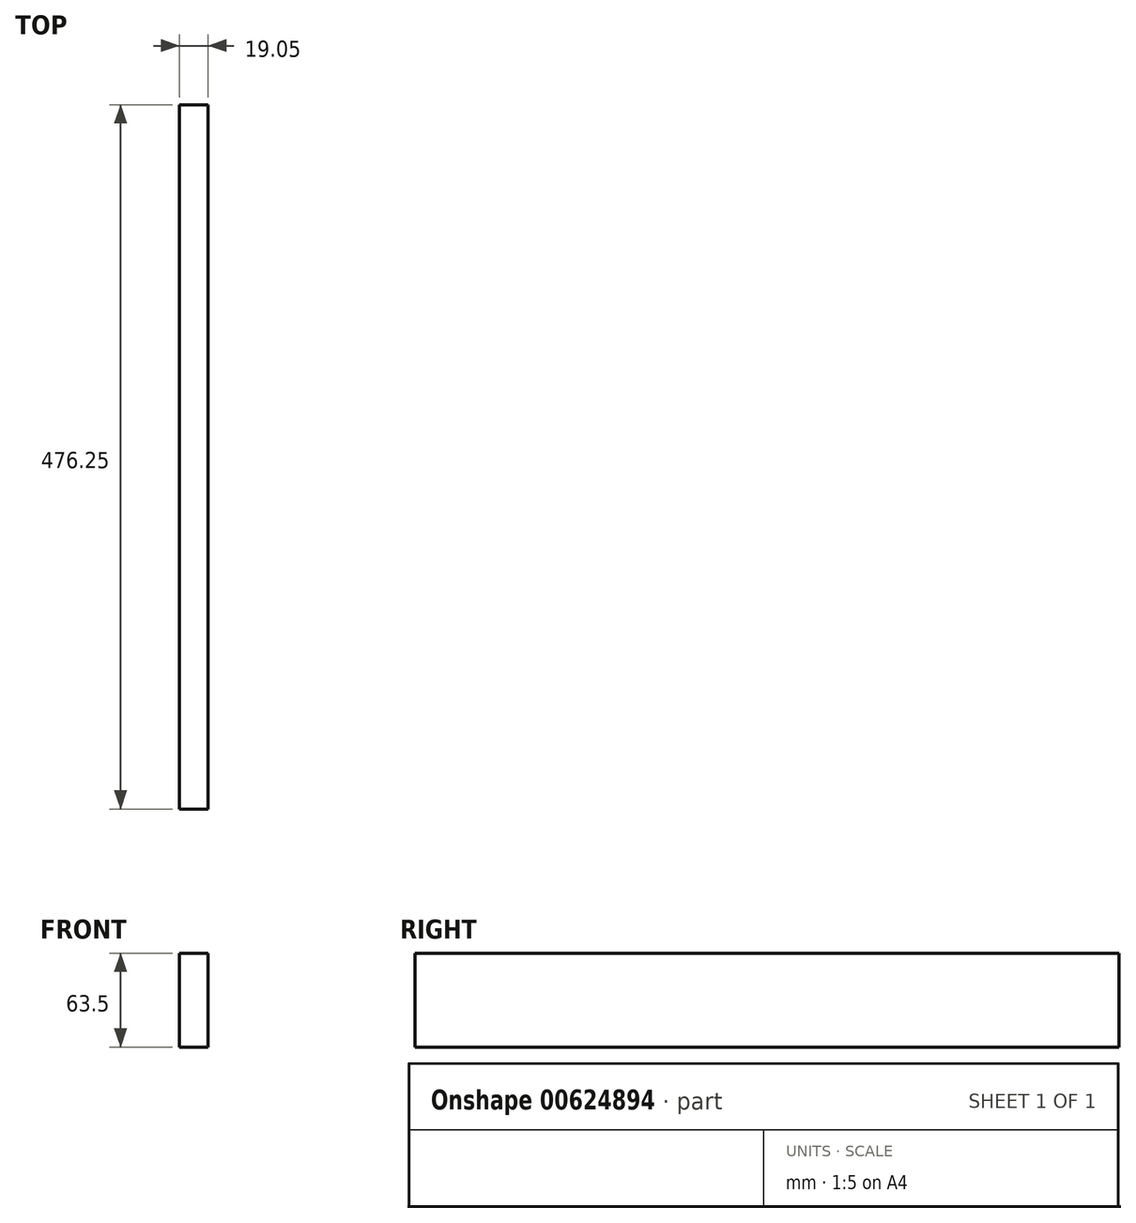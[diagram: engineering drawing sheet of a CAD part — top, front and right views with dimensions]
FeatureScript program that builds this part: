
annotation { "Feature Type Name" : "Feature", "Feature Type Description" : "" }
export const myFeature = defineFeature(function(context is Context, id is Id, definition is map)
    precondition{}
    {
        {
            var Q0;
            Q0=qCreatedBy(makeId("Right.planeOp"),FACE);
            var sketch = newSketch(context, id + "F0", { "sketchPlane" : qUnion([Q0])});
            skLineSegment(sketch, "E0.bottom", {"start": v(0, 0) * mm, "end": v(-476.25, 0) * mm});
            skLineSegment(sketch, "E0.top", {"start": v(0, 63.5) * mm, "end": v(-476.25, 63.5) * mm});
            skLineSegment(sketch, "E0.left", {"start": v(0, 0) * mm, "end": v(0, 63.5) * mm});
            skLineSegment(sketch, "E0.right", {"start": v(-476.25, 0) * mm, "end": v(-476.25, 63.5) * mm});
            skSolve(sketch);
        }
        {
            var Q0;
            Q0=makeQuery(id+"F0.imprint","IMPRINT",FACE,{"disambiguationData":[TD([[makeQuery(id+"F0.imprint","IMPRINT",EDGE,{"derivedFrom":sQuery(id+"F0.wireOp",EDGE,"E0.bottom")}),-1.0]])]});
            extrude(context, id + "F1", {"entities" : qUnion([Q0]), "depth" : 19.05 * mm, "offsetDistance" : 25.4 * mm});
        }
    });
